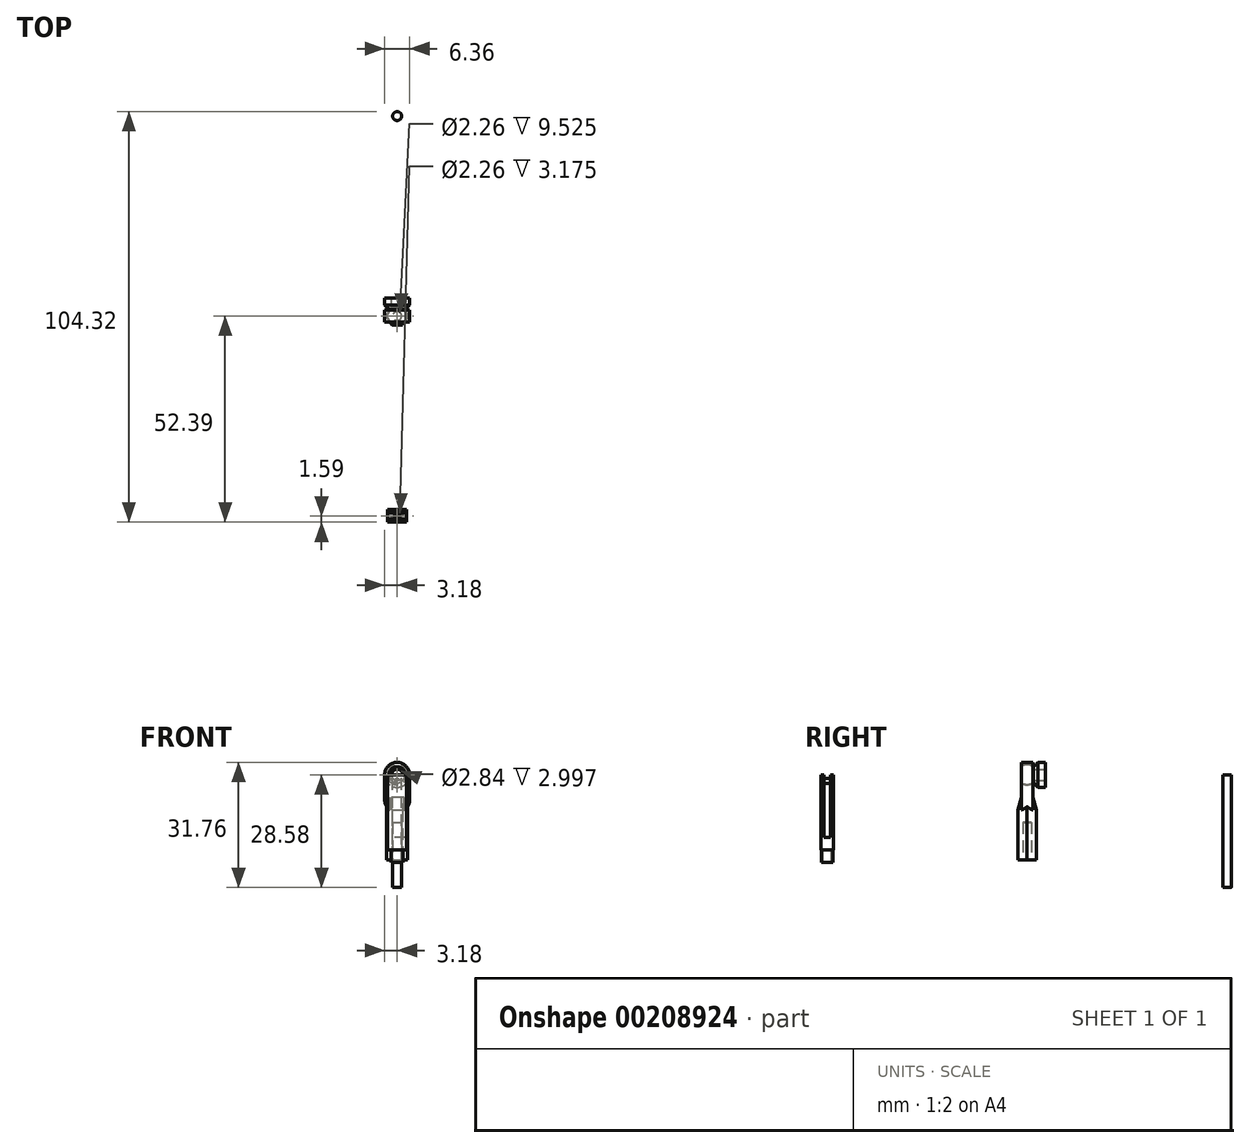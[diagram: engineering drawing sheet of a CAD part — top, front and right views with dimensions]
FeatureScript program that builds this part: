
annotation { "Feature Type Name" : "Feature", "Feature Type Description" : "" }
export const myFeature = defineFeature(function(context is Context, id is Id, definition is map)
    precondition{}
    {
        {
            var Q0;
            Q0=qCreatedBy(makeId("Right.planeOp"),FACE);
            var sketch = newSketch(context, id + "F0", { "sketchPlane" : qUnion([Q0])});
            skLineSegment(sketch, "E0", {"start": v(-1.59, 0) * mm, "end": v(1.59, 0) * mm, "construction": true});
            skLineSegment(sketch, "E1", {"start": v(-1.59, 1.42) * mm, "end": v(1.59, 1.42) * mm});
            skLineSegment(sketch, "E2", {"start": v(1.59, 1.42) * mm, "end": v(1.59, 1.98) * mm});
            skLineSegment(sketch, "E3", {"start": v(-1.59, 1.42) * mm, "end": v(-1.59, 1.98) * mm});
            skArc(sketch, "E4", {"start": v(1.59, 1.98) * mm, "mid": v(0, 2.54) * mm, "end": v(-1.59, 1.98) * mm});
            skLineSegment(sketch, "E5", {"start": v(-1.59, 1.42) * mm, "end": v(-1.59, 0) * mm});
            skLineSegment(sketch, "E6", {"start": v(1.59, 1.42) * mm, "end": v(1.59, 0) * mm});
            skLineSegment(sketch, "E7", {"start": v(1.59, 0) * mm, "end": v(-1.59, 0) * mm});
            skSolve(sketch);
        }
        {
            var Q0;
            Q0=makeQuery(id+"F0.imprint","IMPRINT",FACE,{"disambiguationData":[TD([[makeQuery(id+"F0.imprint","IMPRINT",EDGE,{"derivedFrom":sQuery(id+"F0.wireOp",EDGE,"E1")}),1.0]])]});
            var Q1;
            Q1=sQuery(id+"F0.wireOp",EDGE,"E0");
            revolve(context, id + "F1", {"entities" : qUnion([Q0]), "axis" : qUnion([Q1]), "revolveType" : RevolveType.FULL});
        }
        {
            var Q0;
            Q0=qCreatedBy(makeId("Front.planeOp"),FACE);
            var sketch = newSketch(context, id + "F2", { "sketchPlane" : qUnion([Q0])});
            skArc(sketch, "E8", {"start": v(3.18, 0) * mm, "mid": v(0, 3.18) * mm, "end": v(-3.18, 0) * mm});
            skLineSegment(sketch, "E9", {"start": v(-3.18, 0) * mm, "end": v(-3.18, -6.35) * mm});
            skLineSegment(sketch, "E10", {"start": v(-3.17, -6.35) * mm, "end": v(3.17, -6.35) * mm, "construction": true});
            skLineSegment(sketch, "E11", {"start": v(3.18, -6.35) * mm, "end": v(3.17, 0) * mm});
            skArc(sketch, "E12", {"start": v(-3.17, -6.35) * mm, "mid": v(0, -9.52) * mm, "end": v(3.17, -6.35) * mm});
            skSolve(sketch);
        }
        {
            var Q0;
            Q0=qSketchRegion(id+"F2",true);
            extrude(context, id + "F3", {"entities" : qUnion([Q0]), "endBound" : BoundingType.SYMMETRIC, "depth" : 3 * mm});
        }
        {
            var Q0;
            Q0=makeQuery(id+"F0.imprint","IMPRINT",FACE,{"disambiguationData":[TD([[makeQuery(id+"F0.imprint","IMPRINT",EDGE,{"derivedFrom":sQuery(id+"F0.wireOp",EDGE,"E1")}),-1.0]])]});
            var Q1;
            Q1=makeQuery(id+"F0.imprint","IMPRINT",FACE,{"disambiguationData":[TD([[makeQuery(id+"F0.imprint","IMPRINT",EDGE,{"derivedFrom":sQuery(id+"F0.wireOp",EDGE,"E1")}),1.0]])]});
            var Q2;
            Q2=sQuery(id+"F0.wireOp",EDGE,"E7");
            revolve(context, id + "F4", {"operationType" : NewBodyOperationType.REMOVE, "entities" : qUnion([Q0, Q1]), "axis" : qUnion([Q2]), "revolveType" : RevolveType.FULL, "oppositeDirection" : true});
        }
        {
            var Q0;
            Q0=qCreatedBy(makeId("Top.planeOp"),FACE);
            cPlane(context, id + "F5", {"entities" : qUnion([Q0]), "cplaneType" : CPlaneType.OFFSET, "offset" : 21.59 * mm, "oppositeDirection" : true, "width" : 152.4 * mm, "height" : 152.4 * mm});
        }
        {
            var Q0;
            Q0=qCreatedBy(id+"F5.planeOp",FACE);
            var sketch = newSketch(context, id + "F6", { "sketchPlane" : qUnion([Q0])});
            skCircle(sketch, "E13.cCircle", {"center": v(0, 0) * mm, "radius": 2.67 * mm, "construction": true});
            skLineSegment(sketch, "E13.0", {"start": v(2.67, 0) * mm, "end": v(1.33, -2.3) * mm});
            skLineSegment(sketch, "E13.1", {"start": v(1.33, -2.3) * mm, "end": v(-1.33, -2.3) * mm});
            skLineSegment(sketch, "E13.2", {"start": v(-1.33, -2.3) * mm, "end": v(-2.67, 0) * mm});
            skLineSegment(sketch, "E13.3", {"start": v(-2.67, 0) * mm, "end": v(-1.33, 2.3) * mm});
            skLineSegment(sketch, "E13.4", {"start": v(-1.33, 2.3) * mm, "end": v(1.33, 2.3) * mm});
            skLineSegment(sketch, "E13.5", {"start": v(1.33, 2.3) * mm, "end": v(2.67, 0) * mm});
            skSolve(sketch);
        }
        {
            var Q0;
            Q0=qSketchRegion(id+"F6",true);
            extrude(context, id + "F7", {"entities" : qUnion([Q0]), "operationType" : NewBodyOperationType.ADD, "depth" : 15.88 * mm});
        }
        {
            var Q0;
            Q0=qCreatedBy(makeId("Right.planeOp"),FACE);
            var sketch = newSketch(context, id + "F8", { "sketchPlane" : qUnion([Q0])});
            skLineSegment(sketch, "E14.0", {"start": v(1.5, -6.35) * mm, "end": v(1.5, 0) * mm});
            skLineSegment(sketch, "E15.0", {"start": v(-1.5, -6.35) * mm, "end": v(-1.5, 0) * mm});
            skLineSegment(sketch, "E16.0", {"start": v(1.5, -8.96) * mm, "end": v(1.5, -6.35) * mm});
            skLineSegment(sketch, "E17.0", {"start": v(-1.5, -8.96) * mm, "end": v(-1.5, -6.35) * mm});
            skLineSegment(sketch, "E18.0", {"start": v(-2.3, -5.72) * mm, "end": v(-2.3, -21.59) * mm});
            skLineSegment(sketch, "E19.0", {"start": v(2.3, -5.72) * mm, "end": v(2.3, -21.59) * mm});
            skLineSegment(sketch, "E20", {"start": v(1.5, -8.96) * mm, "end": v(2.3, -8.96) * mm});
            skLineSegment(sketch, "E21", {"start": v(2.3, -8.96) * mm, "end": v(1.5, -5.72) * mm});
            skLineSegment(sketch, "E22", {"start": v(-1.5, -5.72) * mm, "end": v(-2.3, -8.96) * mm});
            skLineSegment(sketch, "E23", {"start": v(-2.3, -8.96) * mm, "end": v(-1.5, -8.96) * mm});
            skLineSegment(sketch, "E24.0", {"start": v(2.3, -5.72) * mm, "end": v(1.5, -5.72) * mm});
            skLineSegment(sketch, "E25.0", {"start": v(-1.5, -5.72) * mm, "end": v(-2.3, -5.72) * mm});
            skSolve(sketch);
        }
        {
            var Q0;
            {var subQ1=sQuery(id+"F8.wireOp",EDGE,"E21");Q0=makeQuery(id+"F8.imprint","IMPRINT",FACE,{"disambiguationData":[TD([[makeQuery(id+"F8.imprint","IMPRINT",EDGE,{"derivedFrom":subQ1}),-1.0]])]});}
            var Q1;
            {var subQ1=sQuery(id+"F8.wireOp",EDGE,"E22");Q1=makeQuery(id+"F8.imprint","IMPRINT",FACE,{"disambiguationData":[TD([[makeQuery(id+"F8.imprint","IMPRINT",EDGE,{"derivedFrom":subQ1}),-1.0]])]});}
            extrude(context, id + "F9", {"entities" : qUnion([Q0, Q1]), "operationType" : NewBodyOperationType.REMOVE, "endBound" : BoundingType.SYMMETRIC, "oppositeDirection" : true, "depth" : 25.4 * mm});
        }
        {
            var Q0;
            Q0=makeQuery(id+"F7.opExtrude","CAP_FACE",FACE,{"disambiguationData":[OSD([sQuery(id+"F6.wireOp",EDGE,"E13.0"),sQuery(id+"F6.wireOp",EDGE,"E13.1"),sQuery(id+"F6.wireOp",EDGE,"E13.2"),sQuery(id+"F6.wireOp",EDGE,"E13.3"),sQuery(id+"F6.wireOp",EDGE,"E13.4"),sQuery(id+"F6.wireOp",EDGE,"E13.5")])],"isStart":true});
            var sketch = newSketch(context, id + "F10", { "sketchPlane" : qUnion([Q0])});
            skCircle(sketch, "E26", {"center": v(0, 0) * mm, "radius": 1.13 * mm});
            skSolve(sketch);
        }
        {
            var Q0;
            Q0=makeQuery(id+"F10.imprint","IMPRINT",FACE,{"disambiguationData":[TD([[makeQuery(id+"F10.imprint","IMPRINT",EDGE,{"derivedFrom":sQuery(id+"F10.wireOp",EDGE,"E26")}),1.0]])]});
            extrude(context, id + "F11", {"entities" : qUnion([Q0]), "operationType" : NewBodyOperationType.REMOVE, "oppositeDirection" : true, "depth" : 9.52 * mm});
        }
        {
            var Q0;
            Q0=qCreatedBy(makeId("Right.planeOp"),FACE);
            var sketch = newSketch(context, id + "F12", { "sketchPlane" : qUnion([Q0])});
            skLineSegment(sketch, "E27.0", {"start": v(1.59, -1.98) * mm, "end": v(1.59, 1.98) * mm});
            skPoint(sketch, "E28", {"position": v(1.59, 0) * mm});
            skLineSegment(sketch, "E29", {"start": v(1.59, -1.98) * mm, "end": v(2.78, -3.18) * mm});
            skLineSegment(sketch, "E30", {"start": v(2.78, -3.17) * mm, "end": v(4.58, -3.17) * mm});
            skLineSegment(sketch, "E31", {"start": v(4.58, -3.18) * mm, "end": v(4.58, -1.42) * mm});
            skLineSegment(sketch, "E32", {"start": v(4.58, -1.42) * mm, "end": v(1.59, -1.42) * mm});
            skLineSegment(sketch, "E33", {"start": v(1.59, -1.42) * mm, "end": v(1.59, -1.98) * mm});
            skSolve(sketch);
        }
        {
            var Q0;
            Q0=makeQuery(id+"F12.imprint","IMPRINT",FACE,{"disambiguationData":[TD([[makeQuery(id+"F12.imprint","IMPRINT",EDGE,{"derivedFrom":sQuery(id+"F12.wireOp",EDGE,"E29")}),1.0]])]});
            var Q1;
            Q1=sQuery(id+"F0.wireOp",EDGE,"E7");
            revolve(context, id + "F13", {"entities" : qUnion([Q0]), "axis" : qUnion([Q1]), "revolveType" : RevolveType.FULL});
        }
        {
            var Q0;
            Q0=qCreatedBy(makeId("Front.planeOp"),FACE);
            cPlane(context, id + "F14", {"entities" : qUnion([Q0]), "cplaneType" : CPlaneType.OFFSET, "offset" : 50.8 * mm, "width" : 152.4 * mm, "height" : 152.4 * mm});
        }
        {
            var Q0;
            Q0=qCreatedBy(makeId("Right.planeOp"),FACE);
            var sketch = newSketch(context, id + "F15", { "sketchPlane" : qUnion([Q0])});
            skLineSegment(sketch, "E34.bottom", {"start": v(-51.6, 0) * mm, "end": v(-50, 0) * mm});
            skLineSegment(sketch, "E34.top", {"start": v(-51.6, -15.88) * mm, "end": v(-50, -15.88) * mm});
            skLineSegment(sketch, "E34.left", {"start": v(-51.6, 0) * mm, "end": v(-51.6, -15.88) * mm});
            skLineSegment(sketch, "E34.right", {"start": v(-50, 0) * mm, "end": v(-50, -15.88) * mm});
            skLineSegment(sketch, "E35.bottom", {"start": v(-52.39, 0) * mm, "end": v(-51.6, 0) * mm});
            skLineSegment(sketch, "E35.top", {"start": v(-52.39, -19.05) * mm, "end": v(-49.21, -19.05) * mm});
            skLineSegment(sketch, "E35.left", {"start": v(-52.39, 0) * mm, "end": v(-52.39, -19.05) * mm});
            skLineSegment(sketch, "E35.right", {"start": v(-49.21, 0) * mm, "end": v(-49.21, -19.05) * mm});
            skLineSegment(sketch, "E36", {"start": v(-50, 0) * mm, "end": v(-49.21, 0) * mm});
            skPoint(sketch, "E37", {"position": v(-50.8, 0) * mm});
            skSolve(sketch);
        }
        {
            var Q0;
            Q0=makeQuery(id+"F15.imprint","IMPRINT",FACE,{"disambiguationData":[TD([[makeQuery(id+"F15.imprint","IMPRINT",EDGE,{"derivedFrom":sQuery(id+"F15.wireOp",EDGE,"E34.top")}),-1.0]])]});
            extrude(context, id + "F16", {"entities" : qUnion([Q0]), "endBound" : BoundingType.SYMMETRIC, "depth" : 4.76 * mm});
        }
        {
            var Q0;
            Q0=makeQuery(id+"F16.opExtrude","SWEPT_FACE",FACE,{"disambiguationData":[OSD([sQuery(id+"F15.wireOp",EDGE,"E35.right")])]});
            var sketch = newSketch(context, id + "F17", { "sketchPlane" : qUnion([Q0])});
            skCircle(sketch, "E38", {"center": v(0, -1.59) * mm, "radius": 0.64 * mm});
            skSolve(sketch);
        }
        {
            var Q0;
            Q0=makeQuery(id+"F17.imprint","IMPRINT",FACE,{"disambiguationData":[TD([[makeQuery(id+"F17.imprint","IMPRINT",EDGE,{"derivedFrom":sQuery(id+"F17.wireOp",EDGE,"E38")}),1.0]])]});
            var Q1;
            Q1=makeQuery(id+"F16.opExtrude","SWEPT_FACE",FACE,{"disambiguationData":[OSD([sQuery(id+"F15.wireOp",EDGE,"E35.left")])]});
            extrude(context, id + "F18", {"entities" : qUnion([Q0]), "operationType" : NewBodyOperationType.ADD, "endBound" : BoundingType.UP_TO_SURFACE, "oppositeDirection" : true, "endBoundEntityFace" : qUnion([Q1]), "depth" : 25.4 * mm});
        }
        {
            var Q0;
            Q0=makeQuery(id+"F16.opExtrude","SWEPT_FACE",FACE,{"disambiguationData":[OSD([sQuery(id+"F15.wireOp",EDGE,"E35.top")])]});
            var sketch = newSketch(context, id + "F19", { "sketchPlane" : qUnion([Q0])});
            skCircle(sketch, "E39", {"center": v(0, 50.8) * mm, "radius": 1.5 * mm});
            skPoint(sketch, "E40", {"position": v(0, 49.21) * mm});
            skPoint(sketch, "E41", {"position": v(2.38, 50.8) * mm});
            skCircle(sketch, "E42", {"center": v(0, 50.8) * mm, "radius": 1.13 * mm});
            skSolve(sketch);
        }
        {
            var Q0;
            Q0=makeQuery(id+"F19.imprint","IMPRINT",FACE,{"disambiguationData":[TD([[makeQuery(id+"F19.imprint","IMPRINT",EDGE,{"derivedFrom":sQuery(id+"F19.wireOp",EDGE,"E39")}),1.0]])]});
            extrude(context, id + "F20", {"entities" : qUnion([Q0]), "operationType" : NewBodyOperationType.ADD, "depth" : 3.17 * mm});
        }
        {
            var Q0;
            Q0=qCreatedBy(makeId("Top.planeOp"),FACE);
            var sketch = newSketch(context, id + "F21", { "sketchPlane" : qUnion([Q0])});
            skCircle(sketch, "E43", {"center": v(0, 50.8) * mm, "radius": 1.13 * mm});
            skSolve(sketch);
        }
        {
            var Q0;
            Q0=qSketchRegion(id+"F21",true);
            extrude(context, id + "F22", {"entities" : qUnion([Q0]), "oppositeDirection" : true, "depth" : 28.57 * mm});
        }
    });
